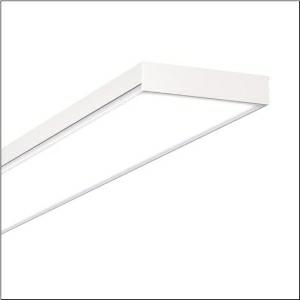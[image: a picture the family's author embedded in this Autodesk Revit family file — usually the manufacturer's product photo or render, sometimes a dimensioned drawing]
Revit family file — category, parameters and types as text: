
# Revit family: apollon_r__31_51mp25wm2341w_ec99
name_source: partatom
category: Lighting Fixtures
units: mm (PartAtom-declared; Revit-internal decimal feet)

## family parameters
Cut with Voids When Loaded = No
Host = Face
Light Source = No
Part Type = Normal
Room Calculation Point = No
Round Connector Dimension = Use Diameter
Shared = No

## types (1)
- Apollon® 31 (1 x LED, 3600 lm, 27 W, 3000K)
    Apparent Load = 27 VA
    CIE Flux Codes = 61 87 97 97 100
    Color Rendering = 80
    Color Temperature = 3000K
    Default Elevation = 1800 mm
    Description = Apollon® 31, office luminaire, primary optical cover: micro prismatic cover, of PMMA, light emission: direct distribution, primary light characteristic: symmetric, installation type: surface-mounted, LED, rated luminous flux: 3.600lm, luminous efficacy: 132lm/W, light colour: 830, colour temperature: 3000K, control gear: ECG Multilumen, with terminal, 3-pole, mains connection: 220..240V, AC, 50/60Hz, rated input power: 27W, housing, of sheet steel, coil coated, traffic white (RAL 9016), length: 1.245mm, width: 200mm, height: 44mm, protection rating (complete): IP20, insulation class (complete): insulation class II (safety insulation), certification: CE, impact resistance: IK02, permissible operating ambient temperature: -20..+40°C, packaging unit: 1 piece
    Height = 44 mm
    Lamp = 1 x LED
    Lamp Light Flux = 3600 lm
    Lamp Power = 27 W
    Lamp count = 1
    Length = 1245 mm
    Luminous efficacy = 133 lm/W
    Manufacturer = Siteco
    ModVariant = No
    Model = 51MP25WM2341W
    Mounting Place = Ceiling
    Mounting Type = Surface mounted
    Number of Poles = 1
    OnlyDefault = Yes
    Power Factor = 1
    Product Name = Apollon® 31
    Product group = office luminaire | ceiling mounted
    ProductGroupID = 302
    Protection Class = Protection class II
    Protection Degree = IP 20
    RLX_Detail_Level = 1
    RlxData = <blob elided: 20705 chars, md5=749e01a4>
    Socket = socket
    Standby Power = 0 W
    System Light Flux = 3600 lm
    System Power = 27 W
    Type Comments = Product without accessories
    Type Image = l_1007095.jpg
    URL = http://relux.com
    VarID = ---
    Voltage = 0 V
    Weight = 0.00 kg
    Width = 200 mm  [stored 0.656168 ft]

note: [stored X ft] marks values corroborated as IEEE doubles in the binary element streams (Revit-internal decimal feet)

## geometry (parser evidence)
native form markers: Blend x4, Sweep x9
no freeform markers — native parametric forms only
